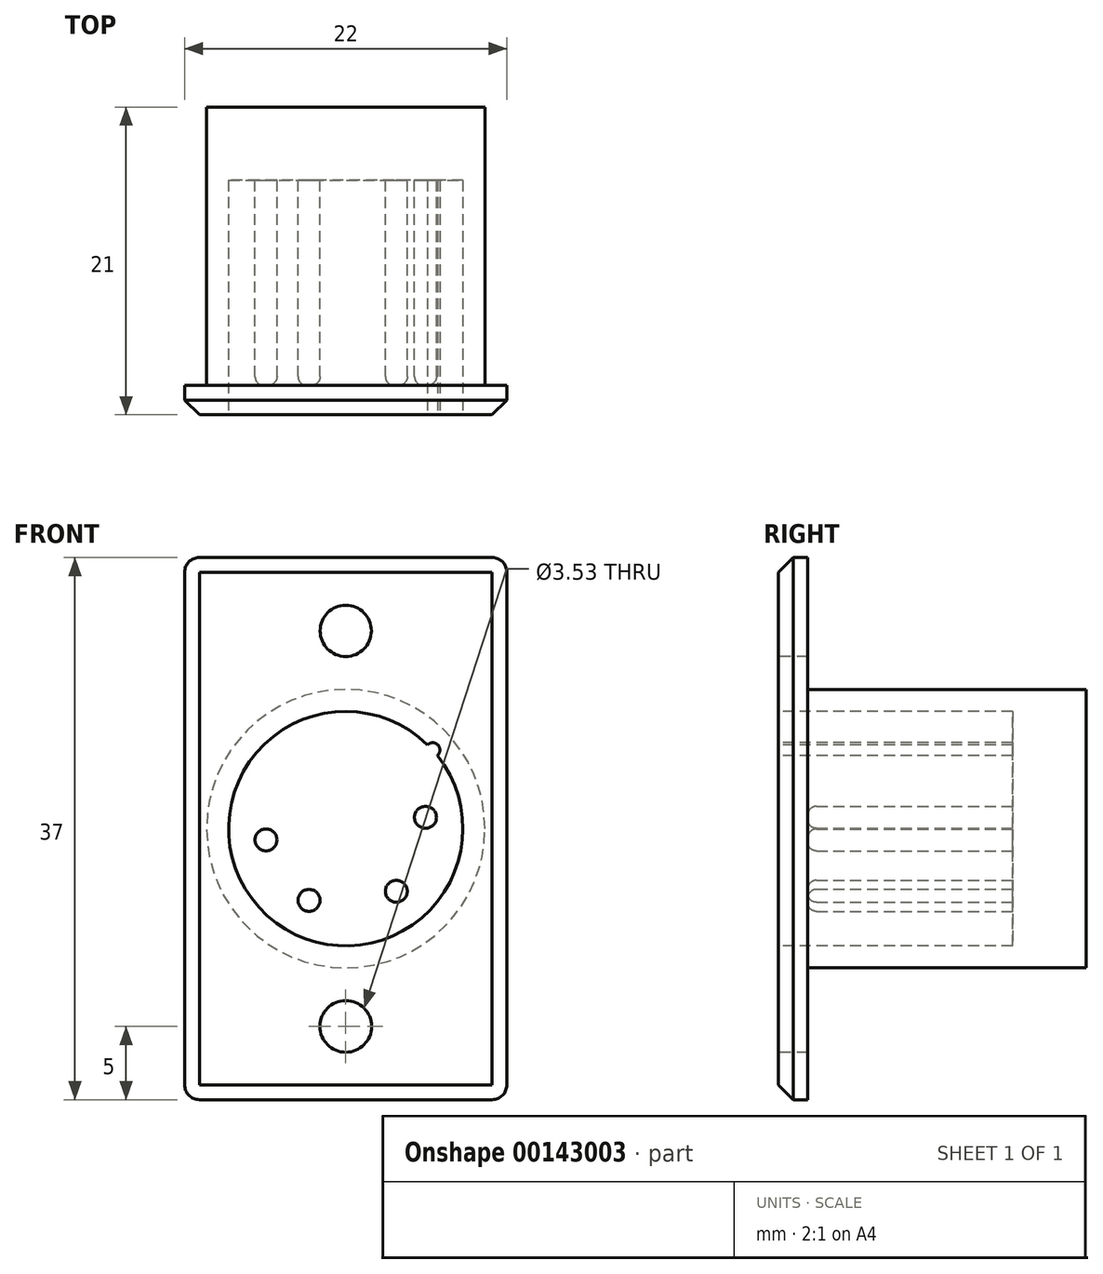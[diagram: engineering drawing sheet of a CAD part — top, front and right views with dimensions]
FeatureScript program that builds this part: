
annotation { "Feature Type Name" : "Feature", "Feature Type Description" : "" }
export const myFeature = defineFeature(function(context is Context, id is Id, definition is map)
    precondition{}
    {
        {
            var Q0;
            Q0=qCreatedBy(makeId("Front.planeOp"),FACE);
            var sketch = newSketch(context, id + "F0", { "sketchPlane" : qUnion([Q0])});
            skLineSegment(sketch, "E0.bottom", {"start": v(1, 0) * mm, "end": v(21, 0) * mm});
            skLineSegment(sketch, "E0.top", {"start": v(1, -37) * mm, "end": v(21, -37) * mm});
            skLineSegment(sketch, "E0.left", {"start": v(0, -1) * mm, "end": v(0, -36) * mm});
            skLineSegment(sketch, "E0.right", {"start": v(22, -1) * mm, "end": v(22, -36) * mm});
            skPoint(sketch, "E1.visualSharp", {"position": v(0, 0) * mm});
            skArc(sketch, "E1.filletArc", {"start": v(1, 0) * mm, "mid": v(0.3, -0.3) * mm, "end": v(0, -1) * mm});
            skPoint(sketch, "E2.visualSharp", {"position": v(22, 0) * mm});
            skArc(sketch, "E2.filletArc", {"start": v(22, -1) * mm, "mid": v(21.7, -0.3) * mm, "end": v(21, 0) * mm});
            skPoint(sketch, "E3.visualSharp", {"position": v(22, -37) * mm});
            skArc(sketch, "E3.filletArc", {"start": v(21, -37) * mm, "mid": v(21.7, -36.7) * mm, "end": v(22, -36) * mm});
            skPoint(sketch, "E4.visualSharp", {"position": v(0, -37) * mm});
            skArc(sketch, "E4.filletArc", {"start": v(0, -36) * mm, "mid": v(0.3, -36.7) * mm, "end": v(1, -37) * mm});
            skSolve(sketch);
        }
        {
            var Q0;
            Q0 = qSketchRegion(id + "F0", true);
            extrude(context, id + "F1", {"entities" : qUnion([Q0]), "depth" : 2 * mm, "offsetDistance" : 25 * mm});
        }
        {
            var Q0;
            Q0=makeQuery(id+"F1.opExtrude","CAP_FACE",FACE,{"disambiguationData":[OSD([sQuery(id+"F0.wireOp",EDGE,"E0.bottom"),sQuery(id+"F0.wireOp",EDGE,"E0.top"),sQuery(id+"F0.wireOp",EDGE,"E0.left"),sQuery(id+"F0.wireOp",EDGE,"E0.right")])],"isStart":false});
            var sketch = newSketch(context, id + "F2", { "sketchPlane" : qUnion([Q0])});
            skPoint(sketch, "E5", {"position": v(11, -18.5) * mm});
            skPoint(sketch, "E5.positionSnap0", {"position": v(0, -18.5) * mm});
            skPoint(sketch, "E5.positionSnap1", {"position": v(11, 0) * mm});
            skCircle(sketch, "E6", {"center": v(11, -18.5) * mm, "radius": 9.5 * mm});
            skSolve(sketch);
        }
        {
            var Q0;
            Q0=makeQuery(id+"F2.imprint","IMPRINT",FACE,{"disambiguationData":[TD([[makeQuery(id+"F2.imprint","IMPRINT",EDGE,{"derivedFrom":sQuery(id+"F2.wireOp",EDGE,"E6")}),1.0]])]});
            var Q1;
            Q1=sQuery(id+"F2.wireOp",EDGE,"E6");
            extrude(context, id + "F3", {"entities" : qUnion([Q0]), "operationType" : NewBodyOperationType.ADD, "surfaceEntities" : qUnion([Q1]), "oppositeDirection" : true, "depth" : 21 * mm, "offsetDistance" : 25 * mm});
        }
        {
            var Q0;
            Q0=makeQuery(id+"F1.opExtrude","CAP_FACE",FACE,{"disambiguationData":[OSD([sQuery(id+"F0.wireOp",EDGE,"E0.bottom"),sQuery(id+"F0.wireOp",EDGE,"E0.top"),sQuery(id+"F0.wireOp",EDGE,"E0.left"),sQuery(id+"F0.wireOp",EDGE,"E0.right")])],"isStart":false});
            var sketch = newSketch(context, id + "F4", { "sketchPlane" : qUnion([Q0])});
            skPoint(sketch, "E7", {"position": v(11, -18.5) * mm});
            skPoint(sketch, "E7.positionSnap0", {"position": v(0, -18.5) * mm});
            skPoint(sketch, "E7.positionSnap1", {"position": v(11, 0) * mm});
            skCircle(sketch, "E8", {"center": v(11, -18.5) * mm, "radius": 8 * mm});
            skCircle(sketch, "E9", {"center": v(16.93, -13.13) * mm, "radius": 0.5 * mm});
            skSolve(sketch);
        }
        {
            var Q0;
            Q0=makeQuery(id+"F4.imprint","IMPRINT",FACE,{"disambiguationData":[TD([[makeQuery(id+"F4.imprint","IMPRINT",EDGE,{"derivedFrom":sQuery(id+"F4.wireOp",EDGE,"E8")}),1.0]])]});
            var Q1;
            {var subQ0=sQuery(id+"F4.wireOp",EDGE,"E9");var subQ1=sQuery(id+"F4.wireOp",EDGE,"E8");var subQ2=makeQuery(id+"F4.imprint","INTERSECT",VERTEX,{"disambiguationData":[OD(0.0)],"derivedFrom":[subQ1,subQ0]});Q1=makeQuery(id+"F4.imprint","IMPRINT",FACE,{"disambiguationData":[TD([[makeQuery(id+"F4.imprint","IMPRINT",EDGE,{"disambiguationData":[TD([[subQ2,1.0]])],"derivedFrom":subQ1}),-1.0]])]});}
            var Q2;
            Q2=sQuery(id+"F4.wireOp",EDGE,"E8");
            extrude(context, id + "F5", {"entities" : qUnion([Q0, Q1]), "operationType" : NewBodyOperationType.REMOVE, "surfaceEntities" : qUnion([Q2]), "oppositeDirection" : true, "depth" : 16 * mm, "offsetDistance" : 25 * mm});
        }
        {
            var Q0;
            Q0=makeQuery(id+"F5.boolean.opBoolean","COPY",FACE,{"derivedFrom":makeQuery(id+"F5.opExtrude","CAP_FACE",FACE,{"disambiguationData":[OSD([sQuery(id+"F4.wireOp",EDGE,"E8"),sQuery(id+"F4.wireOp",EDGE,"E9")])],"isStart":false})});
            var sketch = newSketch(context, id + "F6", { "sketchPlane" : qUnion([Q0])});
            skPoint(sketch, "E10", {"position": v(16.45, -17.73) * mm});
            skPoint(sketch, "E11", {"position": v(14.45, -22.78) * mm});
            skPoint(sketch, "E12", {"position": v(5.55, -19.27) * mm});
            skPoint(sketch, "E13", {"position": v(8.5, -23.4) * mm});
            skPoint(sketch, "E14", {"position": v(11, -18.5) * mm});
            skCircle(sketch, "E15", {"center": v(11, -18.5) * mm, "radius": 5.5 * mm, "construction": true});
            skLineSegment(sketch, "E16", {"start": v(5.5, -18.5) * mm, "end": v(16.5, -18.5) * mm, "construction": true});
            skCircle(sketch, "E17", {"center": v(14.45, -22.78) * mm, "radius": 0.75 * mm});
            skCircle(sketch, "E18", {"center": v(8.5, -23.4) * mm, "radius": 0.75 * mm});
            skCircle(sketch, "E19", {"center": v(5.55, -19.27) * mm, "radius": 0.75 * mm});
            skCircle(sketch, "E20", {"center": v(16.45, -17.73) * mm, "radius": 0.75 * mm});
            skSolve(sketch);
        }
        {
            var Q0;
            Q0 = qSketchRegion(id + "F6", true);
            extrude(context, id + "F7", {"entities" : qUnion([Q0]), "operationType" : NewBodyOperationType.ADD, "depth" : 14 * mm, "offsetDistance" : 25 * mm});
        }
        {
            var Q0;
            Q0=makeQuery(id+"F7.opExtrude","CAP_FACE",FACE,{"disambiguationData":[OSD([sQuery(id+"F6.wireOp",EDGE,"E20")])],"isStart":false});
            var Q1;
            Q1=makeQuery(id+"F7.opExtrude","CAP_EDGE",EDGE,{"disambiguationData":[OSD([sQuery(id+"F6.wireOp",EDGE,"E17")])],"isStart":false});
            var Q2;
            Q2=makeQuery(id+"F7.opExtrude","CAP_FACE",FACE,{"disambiguationData":[OSD([sQuery(id+"F6.wireOp",EDGE,"E18")])],"isStart":false});
            var Q3;
            Q3=makeQuery(id+"F7.opExtrude","CAP_FACE",FACE,{"disambiguationData":[OSD([sQuery(id+"F6.wireOp",EDGE,"E19")])],"isStart":false});
            var Q4;
            Q4=makeQuery(id+"F7.opExtrude","CAP_FACE",FACE,{"disambiguationData":[OSD([sQuery(id+"F6.wireOp",EDGE,"E17")])],"isStart":false});
            fillet(context, id + "F8", {"entities" : qUnion([Q0, Q1, Q2, Q3, Q4]), "radius" : .6 * mm, "tangentPropagation" : true, "allowEdgeOverflow" : false});
        }
        {
            var Q0;
            Q0=makeQuery(id+"F1.opExtrude","CAP_FACE",FACE,{"disambiguationData":[OSD([sQuery(id+"F0.wireOp",EDGE,"E0.bottom"),sQuery(id+"F0.wireOp",EDGE,"E0.top"),sQuery(id+"F0.wireOp",EDGE,"E0.left"),sQuery(id+"F0.wireOp",EDGE,"E0.right")])],"isStart":false});
            var sketch = newSketch(context, id + "F9", { "sketchPlane" : qUnion([Q0])});
            skLineSegment(sketch, "E21", {"start": v(11, 0) * mm, "end": v(11, -37) * mm, "construction": true});
            skPoint(sketch, "E22", {"position": v(11, -5) * mm});
            skPoint(sketch, "E23", {"position": v(11, -32) * mm});
            skCircle(sketch, "E24", {"center": v(11, -5) * mm, "radius": 1.75 * mm});
            skCircle(sketch, "E25", {"center": v(11, -32) * mm, "radius": 1.76 * mm});
            skSolve(sketch);
        }
        {
            var Q0;
            Q0=makeQuery(id+"F9.imprint","IMPRINT",FACE,{"disambiguationData":[TD([[makeQuery(id+"F9.imprint","IMPRINT",EDGE,{"derivedFrom":sQuery(id+"F9.wireOp",EDGE,"E25")}),1.0]])]});
            var Q1;
            Q1=makeQuery(id+"F9.imprint","IMPRINT",FACE,{"disambiguationData":[TD([[makeQuery(id+"F9.imprint","IMPRINT",EDGE,{"derivedFrom":sQuery(id+"F9.wireOp",EDGE,"E24")}),1.0]])]});
            var Q2;
            Q2=sQuery(id+"F9.wireOp",EDGE,"E24");
            var Q3;
            Q3=sQuery(id+"F9.wireOp",EDGE,"E25");
            extrude(context, id + "F10", {"entities" : qUnion([Q0, Q1]), "operationType" : NewBodyOperationType.REMOVE, "surfaceEntities" : qUnion([Q2, Q3]), "endBound" : BoundingType.UP_TO_NEXT, "oppositeDirection" : true, "depth" : 3 * mm, "offsetDistance" : 25 * mm});
        }
        {
            var Q0;
            Q0=makeQuery(id+"F10.boolean.opBoolean","COPY",EDGE,{"derivedFrom":makeQuery(id+"F10.opExtrude","CAP_EDGE",EDGE,{"disambiguationData":[OSD([sQuery(id+"F9.wireOp",EDGE,"E24")])],"isStart":true})});
            var Q1;
            Q1=makeQuery(id+"F10.boolean.opBoolean","COPY",EDGE,{"derivedFrom":makeQuery(id+"F10.opExtrude","CAP_EDGE",EDGE,{"disambiguationData":[OSD([sQuery(id+"F9.wireOp",EDGE,"E25")])],"isStart":true})});
            var Q2;
            Q2=makeQuery(id+"F1.opExtrude","CAP_EDGE",EDGE,{"disambiguationData":[OSD([sQuery(id+"F0.wireOp",EDGE,"E0.right")])],"isStart":false});
            var Q3;
            Q3=makeQuery(id+"F1.opExtrude","CAP_EDGE",EDGE,{"disambiguationData":[OSD([sQuery(id+"F0.wireOp",EDGE,"E0.top")])],"isStart":false});
            var Q4;
            Q4=makeQuery(id+"F1.opExtrude","CAP_EDGE",EDGE,{"disambiguationData":[OSD([sQuery(id+"F0.wireOp",EDGE,"E0.left")])],"isStart":false});
            var Q5;
            Q5=makeQuery(id+"F1.opExtrude","CAP_EDGE",EDGE,{"disambiguationData":[OSD([sQuery(id+"F0.wireOp",EDGE,"E0.bottom")])],"isStart":false});
            chamfer(context, id + "F11", {"entities" : qUnion([Q0, Q1, Q2, Q3, Q4, Q5]), "width" : 1 * mm, "tangentPropagation" : true});
        }
    });
